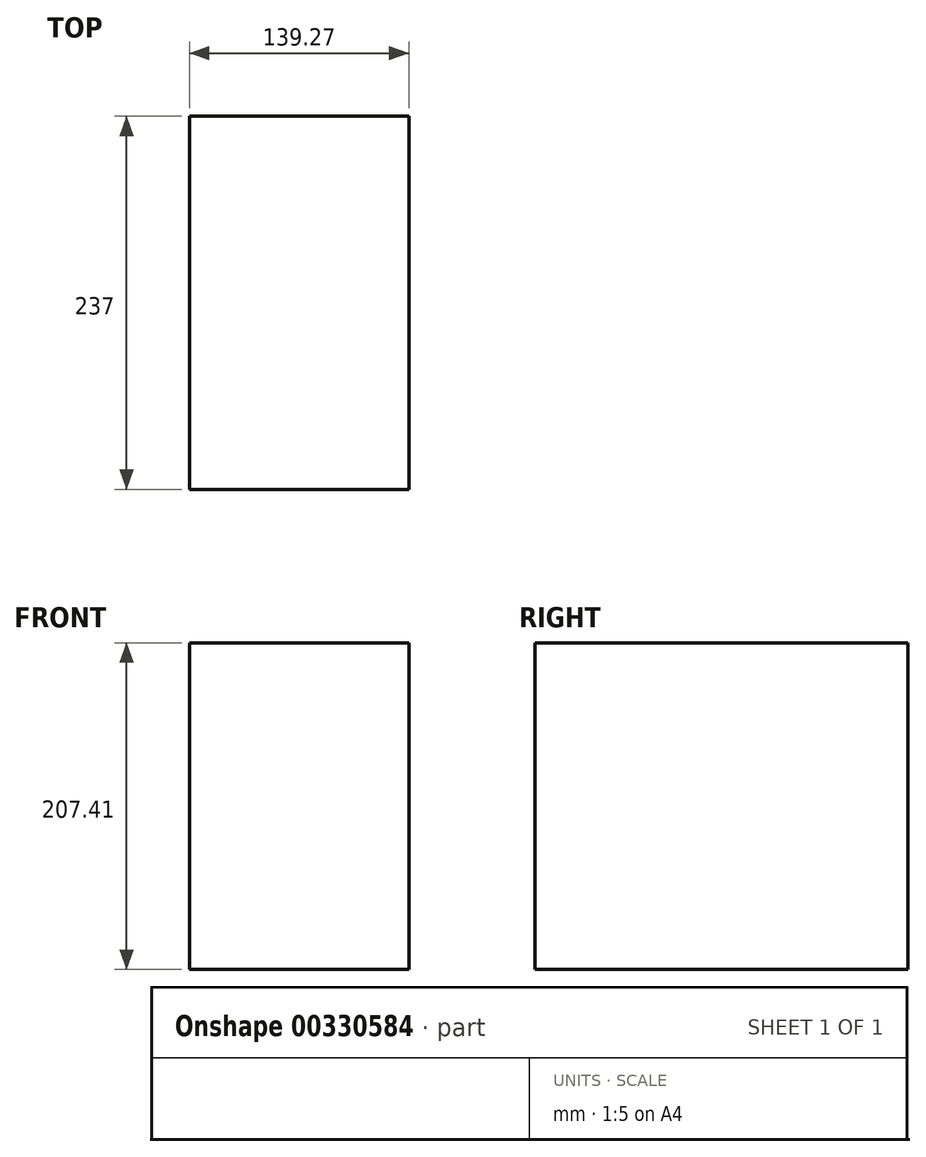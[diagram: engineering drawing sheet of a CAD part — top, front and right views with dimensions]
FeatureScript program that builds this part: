
annotation { "Feature Type Name" : "Feature", "Feature Type Description" : "" }
export const myFeature = defineFeature(function(context is Context, id is Id, definition is map)
    precondition{}
    {
        {
            var Q0;
            Q0=qCreatedBy(makeId("Front.planeOp"),FACE);
            var sketch = newSketch(context, id + "F0", { "sketchPlane" : qUnion([Q0])});
            skLineSegment(sketch, "E0.bottom", {"start": v(0, 0) * mm, "end": v(139.27, 0) * mm});
            skLineSegment(sketch, "E0.top", {"start": v(0, -207.41) * mm, "end": v(139.27, -207.41) * mm});
            skLineSegment(sketch, "E0.left", {"start": v(0, 0) * mm, "end": v(0, -207.41) * mm});
            skLineSegment(sketch, "E0.right", {"start": v(139.27, 0) * mm, "end": v(139.27, -207.41) * mm});
            skSolve(sketch);
        }
        {
            var Q0;
            Q0=makeQuery(id+"F0.imprint","IMPRINT",FACE,{"disambiguationData":[TD([[makeQuery(id+"F0.imprint","IMPRINT",EDGE,{"derivedFrom":sQuery(id+"F0.wireOp",EDGE,"E0.bottom")}),-1.0]])]});
            extrude(context, id + "F1", {"entities" : qUnion([Q0]), "depth" : 237 * mm});
        }
    });
